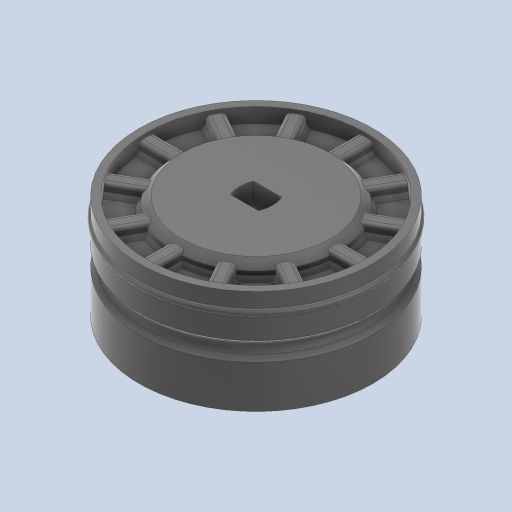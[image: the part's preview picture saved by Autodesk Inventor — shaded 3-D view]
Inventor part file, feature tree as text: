
AUTODESK INVENTOR PART (.ipt)
format: ipt  version: 2023 (Build 270158000, 158)  size: 542,208 bytes
history: native  units: mm
features: extrude x14, sketch x14, chamfer x6, fillet x3
ambient origin geometry x8: Origin, YZ Plane, XZ Plane, XY Plane, X Axis, Y Axis, Z Axis, Center Point
bodies: Body1 (feature_tree)
feature tree (37):
  extrude  "Выдавливание8"  Depth=31.5mm
  extrude  "Выдавливание9"  Depth=5.75mm TaperAngle=0.0deg
  extrude  "Выдавливание10"  Depth=29.5mm
  extrude  "Выдавливание11"  Depth=2.5mm TaperAngle=0.0deg
  extrude  "Выдавливание12"  Depth=5.75mm TaperAngle=0.0deg
  extrude  "Выдавливание13"  Depth=3.6mm TaperAngle=0.0deg
  extrude  "Выдавливание14"  Depth=4.4mm
  extrude  "Выдавливание15"  Depth=4.0mm TaperAngle=0.0deg
  fillet  "Сопряжение13"  Radius=14.0mm
  chamfer  "Фаска7"  [1 undecoded]
  chamfer  "Фаска8"  Distance=22.0mm
  chamfer  "Фаска9"  Distance=2.0mm
  extrude  "Выдавливание17"  Depth=25.75mm
  chamfer  "Фаска11"  Distance=120.0mm Angle=360.0deg
  fillet  "Сопряжение15"  Radius=1.5mm
  extrude  "Выдавливание20"  Depth=0.5mm
  extrude  "Выдавливание21"  Depth=1.0mm TaperAngle=45.0deg
  chamfer  "Фаска12"  Distance=0.5mm Angle=45.0deg
  fillet  "Сопряжение16"  Radius=0.5mm
  extrude  "Выдавливание28"  Depth=6.0mm TaperAngle=0.0deg
  extrude  "Выдавливание29"  Depth=1.0mm TaperAngle=45.0deg
  chamfer  "Фаска13"  Distance=1.0mm
  extrude  "Выдавливание30"  Depth=32.5mm
  sketch  "Эскиз8"
  sketch  "Эскиз9"
  sketch  "Эскиз10"
  sketch  "Эскиз11"
  sketch  "Эскиз12"
  sketch  "Эскиз13"
  sketch  "Эскиз14"
  sketch  "Эскиз15"
  sketch  "Эскиз17"
  sketch  "Эскиз20"
  sketch  "Эскиз21"
  sketch  "Эскиз28"
  sketch  "Эскиз29"
  sketch  "Эскиз30"
note: 1 required parameter value undecoded (feature->parameter linkage not recoverable at this tier; creation-order binding heuristic only, values carry confidence <= 0.55)
